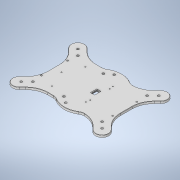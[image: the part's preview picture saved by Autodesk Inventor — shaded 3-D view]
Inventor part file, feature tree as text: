
AUTODESK INVENTOR PART (.ipt)
format: ipt  version: 2020.3 (Build 243373000, 373)  size: 414,208 bytes
history: native  units: mm
features: hole x3, fillet x2, sketch x1, extrude x1
ambient origin geometry x8: Origin, YZ Plane, XZ Plane, XY Plane, X Axis, Y Axis, Z Axis, Center Point
bodies: Body1 (feature_tree)
feature tree (7):
  sketch  "Sketch1"  dims[d0=135.0deg d4=24.6mm d5=12.4mm d9=8.7mm d10=135.0deg d12=6.0mm d13=2.0mm d14=2.0mm d16=20.0mm d23=6.0mm d29=135.0mm d32=15.0mm d33=4.0mm d34=28.4mm d38=4.0mm d40=6.8mm d60=90.0mm d61=135.0deg d70=135.0deg d102=4.0mm d103=0.0mm d104=4.2mm d105=6.0mm d106=4.0mm d107=2.0mm d108=90.0deg d109=8.8mm d110=0.0mm d111=40.0mm d113=22.0mm d114=35.0mm d115=25.0mm d116=31.0mm d117=35.3mm d118=36.0mm d119=18.0mm d120=17.5mm d121=10.0mm d122=20.0mm d123=93.0mm d124=91.7mm d125=1.9mm d126=6.0mm d127=4.0mm d128=2.0mm d129=90.0deg d130=8.0mm d131=0.0mm d153=0.5mm d154=12.0mm d157=6.0mm d158=2.094395mm d159=6.0mm d160=3.8mm d161=2.0mm d162=2.0mm d163=2.0mm d164=2.0mm d165=6.0mm d166=12.0mm d167=5.0mm d168=1.0mm d169=3.0mm d170=45.0mm d171=3.0mm d172=6.0mm d173=4.0mm d174=2.0mm d175=90.0deg d176=8.0mm d177=20.594885mm d178=30.0deg d179=25.0mm d180=10.0mm d182=4.0mm d183=15.0mm]
  extrude  "Extrusion12"  Depth=15.0mm
  hole  "Hole2"  [1 undecoded]
  fillet  "Fillet10"  Radius=8.7mm
  hole  "Hole3"  [1 undecoded]
  fillet  "Fillet15"  Radius=6.0mm
  hole  "Hole4"  [1 undecoded]
note: 3 required parameter values undecoded (feature->parameter linkage not recoverable at this tier; creation-order binding heuristic only, values carry confidence <= 0.55)
